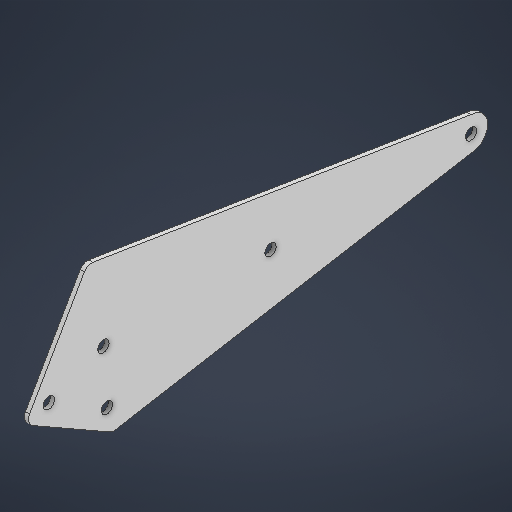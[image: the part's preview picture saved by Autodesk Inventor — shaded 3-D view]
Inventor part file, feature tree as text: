
AUTODESK INVENTOR PART (.ipt)
format: ipt  version: 2025.2 (Build 292293000, 293)  size: 190,464 bytes
history: native  units: in
note: dims shown in document units (in); Inventor stores cm internally (conversion verified against a paired STEP export)
features: extrude x1, sketch x1
ambient origin geometry x8: Origin, YZ Plane, XZ Plane, XY Plane, X Axis, Y Axis, Z Axis, Center Point
bodies: Solid1 (feature_tree)
feature tree (2):
  extrude  "Extrusion1"  Depth=0.0625in TaperAngle=0.0deg
  sketch  "Sketch1"  dims[d0=0.5in d1=1.5in d2=0.172in d3=0.172in d4=0.125in d5=0.125in d6=0.0625in d7=0.0in]
